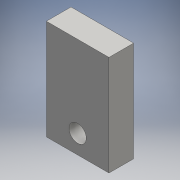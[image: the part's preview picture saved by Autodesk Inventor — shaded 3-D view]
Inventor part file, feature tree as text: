
AUTODESK INVENTOR PART (.ipt)
format: ipt  version: 2016 (Build 200138000, 138)  size: 96,256 bytes
history: native  units: mm
features: extrude x2, sketch x2, projected_geometry x1
ambient origin geometry x8: Origin, YZ Plane, XZ Plane, XY Plane, X Axis, Y Axis, Z Axis, Center Point
bodies: Solid1 (feature_tree)
feature tree (5):
  extrude  "Extrusion1"  Depth=5.0038mm TaperAngle=0.0deg
  extrude  "Extrusion2"  [1 undecoded]
  sketch  "Sketch1"  dims[d0=5.0038mm d1=0.0mm d2=10.16mm d3=0.0mm]
  sketch  "Sketch2"
  projected_geometry  "Projected Loop1"
note: 1 required parameter value undecoded (feature->parameter linkage not recoverable at this tier; creation-order binding heuristic only, values carry confidence <= 0.55)
